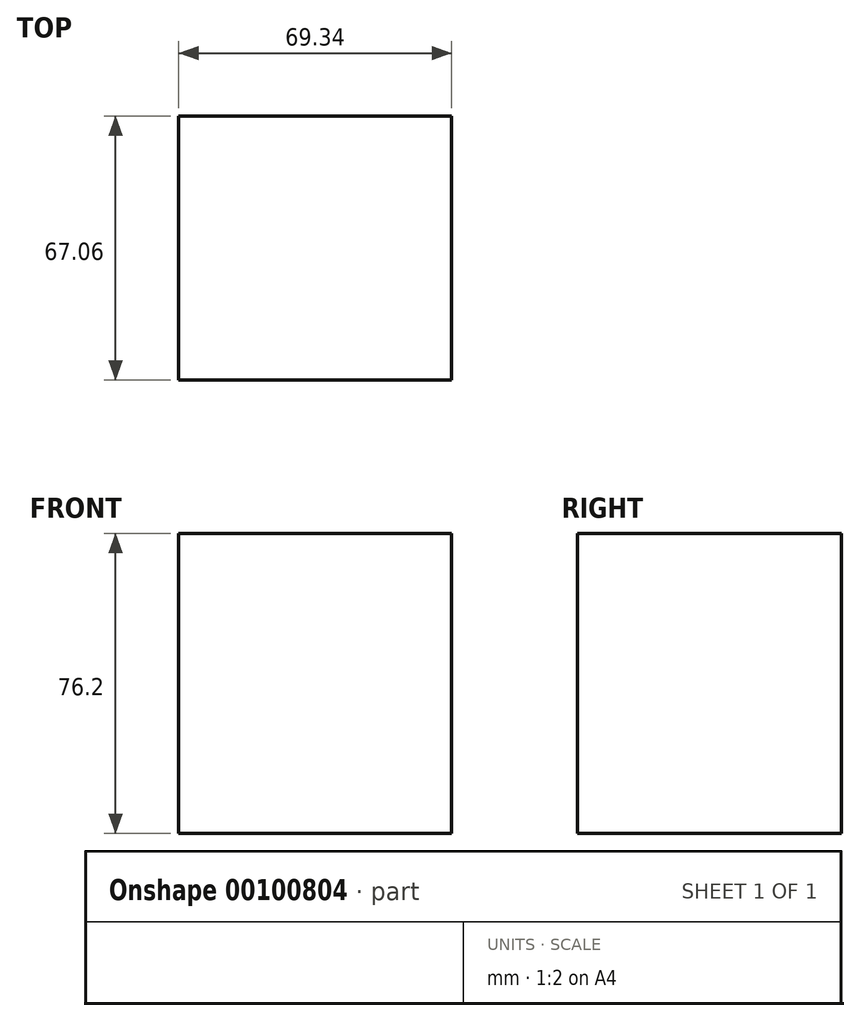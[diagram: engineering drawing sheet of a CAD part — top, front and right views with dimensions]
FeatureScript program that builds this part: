
annotation { "Feature Type Name" : "Feature", "Feature Type Description" : "" }
export const myFeature = defineFeature(function(context is Context, id is Id, definition is map)
    precondition{}
    {
        {
            var Q0;
            Q0=qCreatedBy(makeId("Top.planeOp"),FACE);
            var sketch = newSketch(context, id + "F0", { "sketchPlane" : qUnion([Q0])});
            skLineSegment(sketch, "E0.bottom", {"start": v(34.67, -33.53) * mm, "end": v(-34.67, -33.53) * mm});
            skLineSegment(sketch, "E0.top", {"start": v(34.67, 33.53) * mm, "end": v(-34.67, 33.53) * mm});
            skLineSegment(sketch, "E0.left", {"start": v(34.67, -33.53) * mm, "end": v(34.67, 33.53) * mm});
            skLineSegment(sketch, "E0.right", {"start": v(-34.67, -33.53) * mm, "end": v(-34.67, 33.53) * mm});
            skPoint(sketch, "E0.middle", {"position": v(0, 0) * mm});
            skSolve(sketch);
        }
        {
            var Q0;
            Q0=makeQuery(id+"F0.imprint","IMPRINT",FACE,{"disambiguationData":[TD([[makeQuery(id+"F0.imprint","IMPRINT",EDGE,{"derivedFrom":sQuery(id+"F0.wireOp",EDGE,"E0.bottom")}),-1.0]])]});
            extrude(context, id + "F1", {"entities" : qUnion([Q0]), "depth" : 76.2 * mm});
        }
    });
